# Revit family: METALFIRE_ULTIMATE_D_MF_WHE_1S
name_source: partatom
category: Mechanical Equipment
revit_build: Autodesk Revit 2017 (Build: 20160225_1515(x64)
units: mm (PartAtom-declared; Revit-internal decimal feet)

## family parameters
Always vertical = Yes
Cut with Voids When Loaded = No
Host = Wall
OmniClass Number = 23.75.00.00
OmniClass Title = Climate Control (HVAC)
Part Type = Normal
Room Calculation Point = Yes
Round Connector Dimension = Use Diameter
Shared = No

## types (6) — shared parameters
BIM BADGE = https://bim.archiproducts.com
Description = This generation of room air independent wood fireplaces with liftable door is equipped with a dynamic combustion technique that ensures optimal combustion and high efficiency.
ENERGY EFFICIENCY CLASS = A+
FINISHING MATERIAL = Black painted vermiculite plates - Metalfire
FRAME MATERIAL = Iron - Metalfire
MATERIAL DESCRIPTION = Iron, galvanized steel and vermiculite plates
Manufacturer = Metalfire
Model = Ultime D
OVERALL DEPTH = 619 mm
PRODUCT SHEET = https://www.archiproducts.com
SMOKE EXHAUST = Ø250 mm
TECHNICAL SHEET = https://www.metalfire.eu
URL = https://www.metalfire.eu

## per-type parameters (varying)
| type | CO EMISSION | EFFICIENCY | FINE DUST EMISSION | HEIGHT | OUTPUT | OVERALL HEIGHT | OVERALL WIDTH | PRODUCT CODE | WEIGHT | WIDTH |
| 600 x 500 mm | 0.09% | 80.00% | 33 mg/Nm3 | 506 mm | 13.8 kW | 1561 mm | 860 mm | MF 600-50 WHE 1S | 345.00 kg | 836 mm |
| 600 x 750 mm | 0.07% | 80.00% | 20 mg/Nm3 | 756 mm | 18.8 kW | 2061 mm | 860 mm | MF 600-75 WHE 1S | 368.00 kg | 836 mm |
| 800 x 500 mm | 0.07% | 80.00% | 32 mg/Nm3 | 506 mm | 16.6 kW | 1561 mm | 1060 mm | MF 800-50 WHE 1S | 405.00 kg | 836 mm |
| 800 x 750 mm | 0.08% | 80.00% | 30 mg/Nm3 | 756 mm | 21.5 kW | 2061 mm | 1060 mm | MF 800-75 WHE 1S | 435.00 kg | 836 mm |
| 1050 x 500 mm | 0.06% | 80.00% | 30 mg/Nm3 | 506 mm | 19.4 kW | 1561 mm | 1310 mm | MF 1050-50 WHE 1S | 470.00 kg | 1066 mm |
| 1050 x 750 mm | 0.10% | 77.60% | 26 mg/Nm3 | 756 mm | 27.0 kW | 2061 mm | 1310 mm | MF 1050-75 WHE 1S | 495.00 kg | 1086 mm |

## geometry (parser evidence)
native form markers: Sweep x5
no freeform markers — native parametric forms only
